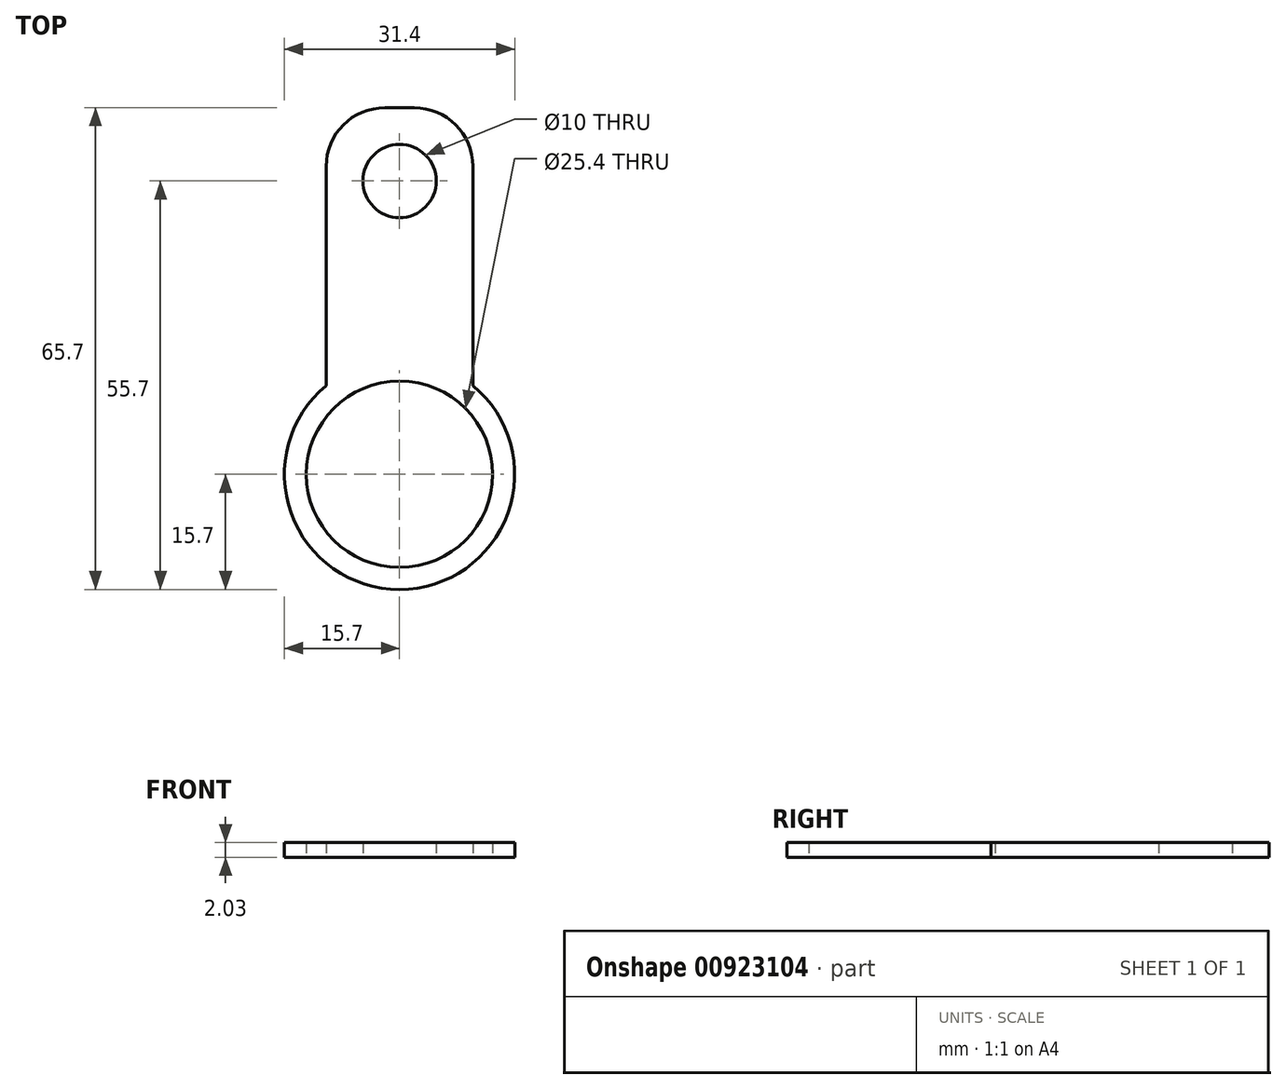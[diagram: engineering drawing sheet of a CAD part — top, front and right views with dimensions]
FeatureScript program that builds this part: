
annotation { "Feature Type Name" : "Feature", "Feature Type Description" : "" }
export const myFeature = defineFeature(function(context is Context, id is Id, definition is map)
    precondition{}
    {
        {
            var Q0;
            Q0=qCreatedBy(makeId("Top.planeOp"),FACE);
            var sketch = newSketch(context, id + "F0", { "sketchPlane" : qUnion([Q0])});
            skLineSegment(sketch, "E0.top", {"start": v(-2, 50) * mm, "end": v(2, 50) * mm});
            skLineSegment(sketch, "E0.left", {"start": v(-10, 12.1) * mm, "end": v(-10, 42) * mm});
            skLineSegment(sketch, "E0.right", {"start": v(10, 12.1) * mm, "end": v(10, 42) * mm});
            skCircle(sketch, "E1", {"center": v(0, 40) * mm, "radius": 5 * mm});
            skLineSegment(sketch, "E2", {"start": v(5, 40) * mm, "end": v(10, 40) * mm, "construction": true});
            skLineSegment(sketch, "E3", {"start": v(0, 45) * mm, "end": v(0, 50) * mm, "construction": true});
            skPoint(sketch, "E4.visualSharp", {"position": v(-10, 50) * mm});
            skArc(sketch, "E4.filletArc", {"start": v(-2, 50) * mm, "mid": v(-7.66, 47.66) * mm, "end": v(-10, 42) * mm});
            skPoint(sketch, "E5.visualSharp", {"position": v(10, 50) * mm});
            skArc(sketch, "E5.filletArc", {"start": v(10, 42) * mm, "mid": v(7.66, 47.66) * mm, "end": v(2, 50) * mm});
            skCircle(sketch, "E6", {"center": v(0, 0) * mm, "radius": 12.7 * mm});
            skArc(sketch, "E7", {"start": v(-10, 12.1) * mm, "mid": v(0, -15.7) * mm, "end": v(10, 12.1) * mm});
            skLineSegment(sketch, "E8", {"start": v(12.7, 0) * mm, "end": v(15.7, 0) * mm, "construction": true});
            skSolve(sketch);
        }
        {
            var Q0;
            Q0 = qSketchRegion(id + "F0", true);
            extrude(context, id + "F1", {"entities" : qUnion([Q0]), "depth" : 2.03 * mm, "offsetDistance" : 25 * mm});
        }
    });
